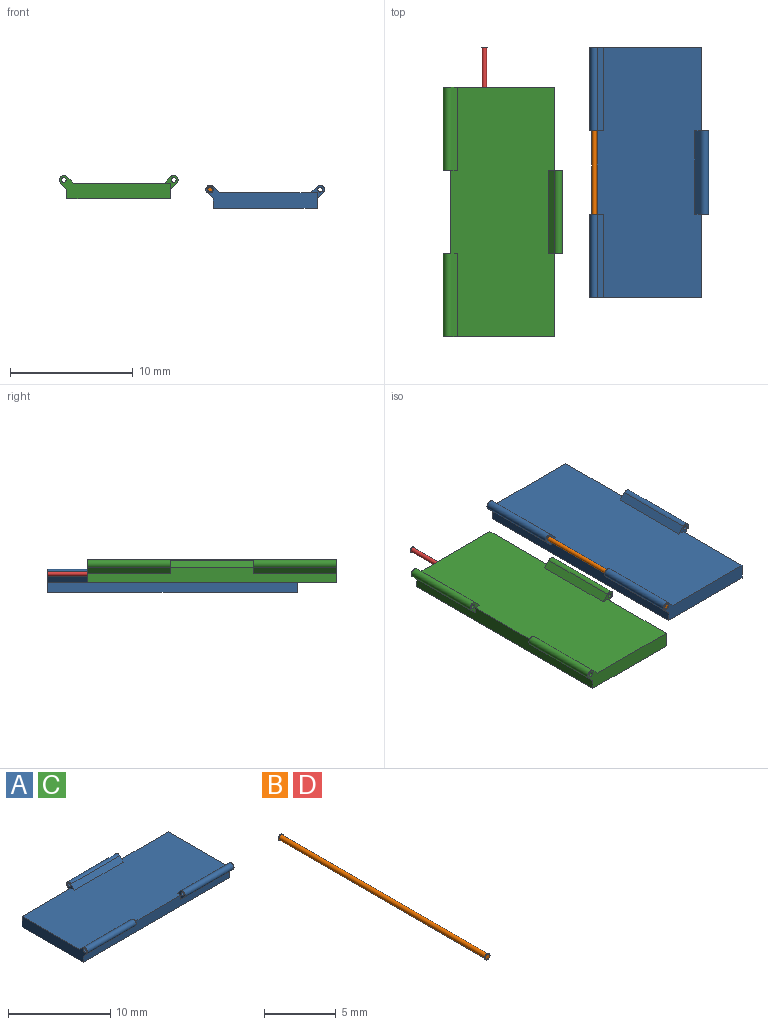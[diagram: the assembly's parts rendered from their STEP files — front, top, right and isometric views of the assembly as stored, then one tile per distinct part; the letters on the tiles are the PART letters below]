
ASSEMBLY  parts=4 mates=1
PART A: 22 faces, bbox 20.3x9.7x1.9 mm
  f0: plane 20.32x1.27mm, normal (0,-1,0), area 19.1mm2, adj f1,f3,f4,f5,f8,f9,f11,f13
  f1: plane 20.32x8.46mm, normal (0,0,1), area 161.6mm2, adj f0,f2,f3,f4,f6,f9,f10,f13
  f2: plane 20.32x1.27mm, normal (0,1,0), area 22.4mm2, adj f1,f3,f4,f5,f16,f17,f18
  f3: plane 9.07x1.88mm, normal (-1,0,0), area 11.2mm2, adj f0,f1,f2,f5,f6,f7,f8,f21
  f4: plane 9.07x1.88mm, normal (1,0,0), area 11.2mm2, adj f0,f1,f2,f5,f10,f11,f12,f20
  f5: plane 20.32x8.46mm, normal (0,0,-1), area 171.9mm2, adj f0,f2,f3,f4
  f6: plane 6.77x0.51mm, normal (0,0.71,0.71), area 4.9mm2, adj f1,f3,f7,f9
  f7: cylinder r=0.36mm len=6.77mm, axis (-1,0,0), area 7.6mm2, adj f3,f6,f8,f9
  f8: plane 6.77x0.5mm, normal (0,-0.71,-0.71), area 4.8mm2, adj f0,f3,f7,f9
  f9: plane 1.12x1.11mm, normal (1,0,0), area 0.5mm2, adj f0,f1,f6,f7,f8,f21
  f10: plane 6.77x0.51mm, normal (0,0.71,0.71), area 4.9mm2, adj f1,f4,f12,f13
  f11: plane 6.77x0.5mm, normal (0,-0.71,-0.71), area 4.8mm2, adj f0,f4,f12,f13
  f12: cylinder r=0.36mm len=6.77mm, axis (1,0,0), area 7.6mm2, adj f4,f10,f11,f13
  f13: plane 1.12x1.11mm, normal (-1,0,0), area 0.5mm2, adj f0,f1,f10,f11,f12,f20
  f14: plane 6.77x0.5mm, normal (0,-0.71,0.7), area 4.8mm2, adj f1,f15,f17,f18
  f15: cylinder r=0.36mm len=6.77mm, axis (1,0,0), area 7.6mm2, adj f14,f16,f17,f18
  f16: plane 6.77x0.51mm, normal (0,0.71,-0.7), area 4.8mm2, adj f2,f15,f17,f18
  f17: plane 1.11x1.11mm, normal (-1,0,0), area 0.5mm2, adj f1,f2,f14,f15,f16,f19
  f18: plane 1.11x1.11mm, normal (1,0,0), area 0.5mm2, adj f1,f2,f14,f15,f16,f19
  f19: cylinder r=0.19mm len=6.77mm, axis (-1,0,0), area 8.1mm2, adj f17,f18
  f20: cylinder r=0.19mm len=6.77mm, axis (-1,0,0), area 8.1mm2, adj f4,f13
  f21: cylinder r=0.19mm len=6.77mm, axis (-1,0,0), area 8.1mm2, adj f3,f9
PART B: 7 faces, bbox 0.6x20.4x0.6 mm
  f0: cylinder r=0.19mm len=20.32mm, axis (0,1,0), area 24.3mm2, adj f2,f4
  f1: plane 0.46x0.46mm, normal (0,-1,0), area 0.2mm2, adj f6
  f2: plane 0.51x0.51mm, normal (0,1,0), area 0.1mm2, adj f0,f6
  f3: plane 0.46x0.46mm, normal (0,1,0), area 0.2mm2, adj f5
  f4: plane 0.51x0.51mm, normal (0,-1,0), area 0.1mm2, adj f0,f5
  f5: torus R=0.23mm, axis (0,1,0), area 0.1mm2, adj f3,f4
  f6: torus R=0.23mm, axis (0,-1,0), area 0.1mm2, adj f1,f2
PART C: same geometry as A
PART D: same geometry as B
PLACE A rot(axis=(0,0,-1),90deg) t=(-4.07,5.41,-17.09)mm
PLACE B t=(-4.32,5.41,-15.53)mm
PLACE C rot(axis=(0,0,-1),90deg) t=(-16,2.2,-16.3)mm
PLACE D t=(-13.28,5.41,-15.53)mm
MATE fastened B.f0 <-> A.f7  axis (0,1,0) through (-4.32,-14.91,-15.57)mm
